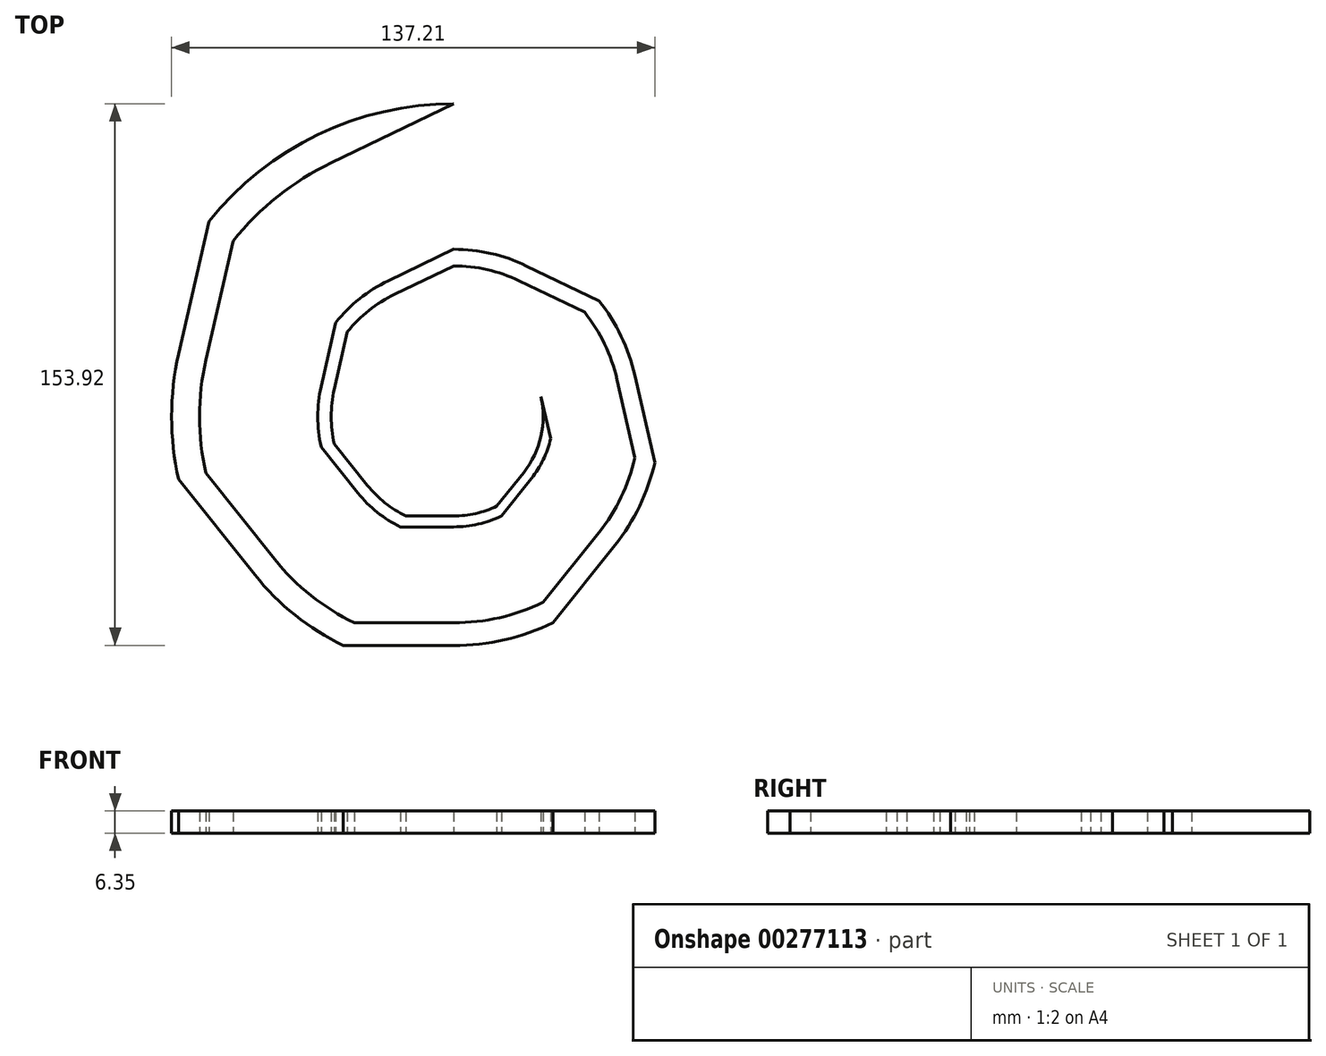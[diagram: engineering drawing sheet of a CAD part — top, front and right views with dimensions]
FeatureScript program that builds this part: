
annotation { "Feature Type Name" : "Feature", "Feature Type Description" : "" }
export const myFeature = defineFeature(function(context is Context, id is Id, definition is map)
    precondition{}
    {
        {
            var Q0;
            Q0=qCreatedBy(makeId("Top.planeOp"),FACE);
            var sketch = newSketch(context, id + "F0", { "sketchPlane" : qUnion([Q0])});
            skCircle(sketch, "E0", {"center": v(0, 0) * mm, "radius": 88.9 * mm});
            skCircle(sketch, "E1.cCircle", {"center": v(0, 0) * mm, "radius": 88.9 * mm, "construction": true});
            skLineSegment(sketch, "E1.0", {"start": v(0, 88.9) * mm, "end": v(69.5, 55.43) * mm});
            skLineSegment(sketch, "E1.1", {"start": v(69.5, 55.43) * mm, "end": v(86.67, -19.78) * mm});
            skLineSegment(sketch, "E1.2", {"start": v(86.67, -19.78) * mm, "end": v(38.57, -80.1) * mm});
            skLineSegment(sketch, "E1.3", {"start": v(38.57, -80.1) * mm, "end": v(-38.57, -80.1) * mm});
            skLineSegment(sketch, "E1.4", {"start": v(-38.57, -80.1) * mm, "end": v(-86.67, -19.78) * mm});
            skLineSegment(sketch, "E1.5", {"start": v(-86.67, -19.78) * mm, "end": v(-69.5, 55.43) * mm});
            skLineSegment(sketch, "E1.6", {"start": v(-69.5, 55.43) * mm, "end": v(0, 88.9) * mm});
            skCircle(sketch, "E2", {"center": v(0, 0) * mm, "radius": 80.1 * mm});
            skCircle(sketch, "E3.cCircle", {"center": v(0, 0) * mm, "radius": 80.1 * mm, "construction": true});
            skLineSegment(sketch, "E3.0", {"start": v(0, 80.1) * mm, "end": v(62.62, 49.94) * mm});
            skLineSegment(sketch, "E3.1", {"start": v(62.62, 49.94) * mm, "end": v(78.09, -17.82) * mm});
            skLineSegment(sketch, "E3.2", {"start": v(78.09, -17.82) * mm, "end": v(34.75, -72.16) * mm});
            skLineSegment(sketch, "E3.3", {"start": v(34.75, -72.16) * mm, "end": v(-34.75, -72.16) * mm});
            skLineSegment(sketch, "E3.4", {"start": v(-34.75, -72.16) * mm, "end": v(-78.09, -17.82) * mm});
            skLineSegment(sketch, "E3.5", {"start": v(-78.09, -17.82) * mm, "end": v(-62.62, 49.94) * mm});
            skLineSegment(sketch, "E3.6", {"start": v(-62.62, 49.94) * mm, "end": v(0, 80.1) * mm});
            skCircle(sketch, "E4", {"center": v(0, 0) * mm, "radius": 72.16 * mm});
            skCircle(sketch, "E5.cCircle", {"center": v(0, 0) * mm, "radius": 72.16 * mm, "construction": true});
            skLineSegment(sketch, "E5.0", {"start": v(0, 72.16) * mm, "end": v(56.42, 45) * mm});
            skLineSegment(sketch, "E5.1", {"start": v(56.42, 45) * mm, "end": v(70.35, -16.06) * mm});
            skLineSegment(sketch, "E5.2", {"start": v(70.35, -16.06) * mm, "end": v(31.31, -65.02) * mm});
            skLineSegment(sketch, "E5.3", {"start": v(31.31, -65.02) * mm, "end": v(-31.31, -65.02) * mm});
            skLineSegment(sketch, "E5.4", {"start": v(-31.31, -65.02) * mm, "end": v(-70.35, -16.06) * mm});
            skLineSegment(sketch, "E5.5", {"start": v(-70.35, -16.06) * mm, "end": v(-56.42, 45) * mm});
            skLineSegment(sketch, "E5.6", {"start": v(-56.42, 45) * mm, "end": v(0, 72.16) * mm});
            skCircle(sketch, "E6", {"center": v(0, 0) * mm, "radius": 65.02 * mm});
            skCircle(sketch, "E7.cCircle", {"center": v(0, 0) * mm, "radius": 65.02 * mm, "construction": true});
            skLineSegment(sketch, "E7.0", {"start": v(0, 65.02) * mm, "end": v(50.83, 40.54) * mm});
            skLineSegment(sketch, "E7.1", {"start": v(50.83, 40.54) * mm, "end": v(63.39, -14.47) * mm});
            skLineSegment(sketch, "E7.2", {"start": v(63.39, -14.47) * mm, "end": v(28.21, -58.58) * mm});
            skLineSegment(sketch, "E7.3", {"start": v(28.21, -58.58) * mm, "end": v(-28.21, -58.58) * mm});
            skLineSegment(sketch, "E7.4", {"start": v(-28.21, -58.58) * mm, "end": v(-63.39, -14.47) * mm});
            skLineSegment(sketch, "E7.5", {"start": v(-63.39, -14.47) * mm, "end": v(-50.83, 40.54) * mm});
            skLineSegment(sketch, "E7.6", {"start": v(-50.83, 40.54) * mm, "end": v(0, 65.02) * mm});
            skCircle(sketch, "E8", {"center": v(0, 0) * mm, "radius": 58.58 * mm});
            skCircle(sketch, "E9.cCircle", {"center": v(0, 0) * mm, "radius": 58.58 * mm, "construction": true});
            skLineSegment(sketch, "E9.0", {"start": v(0, 58.58) * mm, "end": v(45.8, 36.52) * mm});
            skLineSegment(sketch, "E9.1", {"start": v(45.8, 36.52) * mm, "end": v(57.11, -13.04) * mm});
            skLineSegment(sketch, "E9.2", {"start": v(57.11, -13.04) * mm, "end": v(25.42, -52.78) * mm});
            skLineSegment(sketch, "E9.3", {"start": v(25.42, -52.78) * mm, "end": v(-25.42, -52.78) * mm});
            skLineSegment(sketch, "E9.4", {"start": v(-25.42, -52.78) * mm, "end": v(-57.11, -13.04) * mm});
            skLineSegment(sketch, "E9.5", {"start": v(-57.11, -13.04) * mm, "end": v(-45.8, 36.52) * mm});
            skLineSegment(sketch, "E9.6", {"start": v(-45.8, 36.52) * mm, "end": v(0, 58.58) * mm});
            skCircle(sketch, "E10", {"center": v(0, 0) * mm, "radius": 52.78 * mm});
            skCircle(sketch, "E11.cCircle", {"center": v(0, 0) * mm, "radius": 52.78 * mm, "construction": true});
            skLineSegment(sketch, "E11.0", {"start": v(0, 52.78) * mm, "end": v(41.26, 32.9) * mm});
            skLineSegment(sketch, "E11.1", {"start": v(41.26, 32.9) * mm, "end": v(51.45, -11.74) * mm});
            skLineSegment(sketch, "E11.2", {"start": v(51.45, -11.74) * mm, "end": v(22.9, -47.55) * mm});
            skLineSegment(sketch, "E11.3", {"start": v(22.9, -47.55) * mm, "end": v(-22.9, -47.55) * mm});
            skLineSegment(sketch, "E11.4", {"start": v(-22.9, -47.55) * mm, "end": v(-51.45, -11.74) * mm});
            skLineSegment(sketch, "E11.5", {"start": v(-51.45, -11.74) * mm, "end": v(-41.26, 32.9) * mm});
            skLineSegment(sketch, "E11.6", {"start": v(-41.26, 32.9) * mm, "end": v(0, 52.78) * mm});
            skCircle(sketch, "E12", {"center": v(0, 0) * mm, "radius": 47.55 * mm});
            skCircle(sketch, "E13.cCircle", {"center": v(0, 0) * mm, "radius": 47.55 * mm, "construction": true});
            skLineSegment(sketch, "E13.0", {"start": v(0, 47.55) * mm, "end": v(37.18, 29.65) * mm});
            skLineSegment(sketch, "E13.1", {"start": v(37.18, 29.65) * mm, "end": v(46.36, -10.58) * mm});
            skLineSegment(sketch, "E13.2", {"start": v(46.36, -10.58) * mm, "end": v(20.63, -42.84) * mm});
            skLineSegment(sketch, "E13.3", {"start": v(20.63, -42.84) * mm, "end": v(-20.63, -42.84) * mm});
            skLineSegment(sketch, "E13.4", {"start": v(-20.63, -42.84) * mm, "end": v(-46.36, -10.58) * mm});
            skLineSegment(sketch, "E13.5", {"start": v(-46.36, -10.58) * mm, "end": v(-37.18, 29.65) * mm});
            skLineSegment(sketch, "E13.6", {"start": v(-37.18, 29.65) * mm, "end": v(0, 47.55) * mm});
            skCircle(sketch, "E14", {"center": v(0, 0) * mm, "radius": 42.84 * mm});
            skCircle(sketch, "E15.cCircle", {"center": v(0, 0) * mm, "radius": 42.84 * mm, "construction": true});
            skLineSegment(sketch, "E15.0", {"start": v(0, 42.84) * mm, "end": v(33.5, 26.71) * mm});
            skLineSegment(sketch, "E15.1", {"start": v(33.5, 26.71) * mm, "end": v(41.77, -9.53) * mm});
            skLineSegment(sketch, "E15.2", {"start": v(41.77, -9.53) * mm, "end": v(18.59, -38.6) * mm});
            skLineSegment(sketch, "E15.3", {"start": v(18.59, -38.6) * mm, "end": v(-18.59, -38.6) * mm});
            skLineSegment(sketch, "E15.4", {"start": v(-18.59, -38.6) * mm, "end": v(-41.77, -9.53) * mm});
            skLineSegment(sketch, "E15.5", {"start": v(-41.77, -9.53) * mm, "end": v(-33.5, 26.71) * mm});
            skLineSegment(sketch, "E15.6", {"start": v(-33.5, 26.71) * mm, "end": v(0, 42.84) * mm});
            skCircle(sketch, "E16", {"center": v(0, 0) * mm, "radius": 38.6 * mm});
            skCircle(sketch, "E17.cCircle", {"center": v(0, 0) * mm, "radius": 38.6 * mm, "construction": true});
            skLineSegment(sketch, "E17.0", {"start": v(0, 38.6) * mm, "end": v(30.18, 24.07) * mm});
            skLineSegment(sketch, "E17.1", {"start": v(30.18, 24.07) * mm, "end": v(37.63, -8.59) * mm});
            skLineSegment(sketch, "E17.2", {"start": v(37.63, -8.59) * mm, "end": v(16.75, -34.78) * mm});
            skLineSegment(sketch, "E17.3", {"start": v(16.75, -34.78) * mm, "end": v(-16.75, -34.78) * mm});
            skLineSegment(sketch, "E17.4", {"start": v(-16.75, -34.78) * mm, "end": v(-37.63, -8.59) * mm});
            skLineSegment(sketch, "E17.5", {"start": v(-37.63, -8.59) * mm, "end": v(-30.18, 24.07) * mm});
            skLineSegment(sketch, "E17.6", {"start": v(-30.18, 24.07) * mm, "end": v(0, 38.6) * mm});
            skCircle(sketch, "E18", {"center": v(0, 0) * mm, "radius": 34.78 * mm});
            skCircle(sketch, "E19.cCircle", {"center": v(0, 0) * mm, "radius": 34.78 * mm, "construction": true});
            skLineSegment(sketch, "E19.0", {"start": v(0, 34.78) * mm, "end": v(27.19, 21.68) * mm});
            skLineSegment(sketch, "E19.1", {"start": v(27.19, 21.68) * mm, "end": v(33.9, -7.74) * mm});
            skLineSegment(sketch, "E19.2", {"start": v(33.9, -7.74) * mm, "end": v(15.09, -31.33) * mm});
            skLineSegment(sketch, "E19.3", {"start": v(15.09, -31.33) * mm, "end": v(-15.09, -31.33) * mm});
            skLineSegment(sketch, "E19.4", {"start": v(-15.09, -31.33) * mm, "end": v(-33.9, -7.74) * mm});
            skLineSegment(sketch, "E19.5", {"start": v(-33.9, -7.74) * mm, "end": v(-27.19, 21.68) * mm});
            skLineSegment(sketch, "E19.6", {"start": v(-27.19, 21.68) * mm, "end": v(0, 34.78) * mm});
            skCircle(sketch, "E20", {"center": v(0, 0) * mm, "radius": 31.33 * mm});
            skCircle(sketch, "E21.cCircle", {"center": v(0, 0) * mm, "radius": 31.33 * mm, "construction": true});
            skLineSegment(sketch, "E21.0", {"start": v(0, 31.33) * mm, "end": v(24.5, 19.54) * mm});
            skLineSegment(sketch, "E21.1", {"start": v(24.5, 19.54) * mm, "end": v(30.55, -6.97) * mm});
            skLineSegment(sketch, "E21.2", {"start": v(30.55, -6.97) * mm, "end": v(13.6, -28.23) * mm});
            skLineSegment(sketch, "E21.3", {"start": v(13.6, -28.23) * mm, "end": v(-13.6, -28.23) * mm});
            skLineSegment(sketch, "E21.4", {"start": v(-13.6, -28.23) * mm, "end": v(-30.55, -6.97) * mm});
            skLineSegment(sketch, "E21.5", {"start": v(-30.55, -6.97) * mm, "end": v(-24.5, 19.54) * mm});
            skLineSegment(sketch, "E21.6", {"start": v(-24.5, 19.54) * mm, "end": v(0, 31.33) * mm});
            skCircle(sketch, "E22", {"center": v(0, 0) * mm, "radius": 28.23 * mm});
            skCircle(sketch, "E23.cCircle", {"center": v(0, 0) * mm, "radius": 28.23 * mm, "construction": true});
            skLineSegment(sketch, "E23.0", {"start": v(0, 28.23) * mm, "end": v(22.07, 17.6) * mm});
            skLineSegment(sketch, "E23.1", {"start": v(22.07, 17.6) * mm, "end": v(27.52, -6.28) * mm});
            skLineSegment(sketch, "E23.2", {"start": v(27.52, -6.28) * mm, "end": v(12.25, -25.43) * mm});
            skLineSegment(sketch, "E23.3", {"start": v(12.25, -25.43) * mm, "end": v(-12.25, -25.43) * mm});
            skLineSegment(sketch, "E23.4", {"start": v(-12.25, -25.43) * mm, "end": v(-27.52, -6.28) * mm});
            skLineSegment(sketch, "E23.5", {"start": v(-27.52, -6.28) * mm, "end": v(-22.07, 17.6) * mm});
            skLineSegment(sketch, "E23.6", {"start": v(-22.07, 17.6) * mm, "end": v(0, 28.23) * mm});
            skCircle(sketch, "E24", {"center": v(0, 0) * mm, "radius": 25.43 * mm});
            skSolve(sketch);
        }
        {
            var Q0;
            {var subQ0=sQuery(id+"F0.wireOp",EDGE,"E1.6");var subQ4=makeQuery(id+"F0.imprint","INTERSECT",VERTEX,{"derivedFrom":[subQ0,sQuery(id+"F0.wireOp",EDGE,"E2")]});Q0=makeQuery(id+"F0.imprint","IMPRINT",FACE,{"disambiguationData":[TD([[makeQuery(id+"F0.imprint","IMPRINT",EDGE,{"disambiguationData":[TD([[subQ4,1.0]])],"derivedFrom":subQ0}),1.0]])]});}
            var Q1;
            {var subQ1=sQuery(id+"F0.wireOp",EDGE,"E1.5");var subQ3=sQuery(id+"F0.wireOp",EDGE,"E2");var subQ4=makeQuery(id+"F0.imprint","INTERSECT",VERTEX,{"derivedFrom":[subQ1,subQ3]});Q1=makeQuery(id+"F0.imprint","IMPRINT",FACE,{"disambiguationData":[TD([[makeQuery(id+"F0.imprint","IMPRINT",EDGE,{"disambiguationData":[TD([[subQ4,-1.0]])],"derivedFrom":subQ1}),-1.0]])]});}
            var Q2;
            {var subQ1=sQuery(id+"F0.wireOp",EDGE,"E2");var subQ3=makeQuery(id+"F0.imprint","INTERSECT",VERTEX,{"derivedFrom":[sQuery(id+"F0.wireOp",EDGE,"E1.5"),subQ1]});Q2=makeQuery(id+"F0.imprint","IMPRINT",FACE,{"disambiguationData":[TD([[makeQuery(id+"F0.imprint","IMPRINT",EDGE,{"disambiguationData":[TD([[subQ3,1.0]])],"derivedFrom":subQ1}),1.0]])]});}
            var Q3;
            {var subQ1=sQuery(id+"F0.wireOp",EDGE,"E3.4");var subQ3=sQuery(id+"F0.wireOp",EDGE,"E4");var subQ4=makeQuery(id+"F0.imprint","INTERSECT",VERTEX,{"derivedFrom":[subQ1,subQ3]});Q3=makeQuery(id+"F0.imprint","IMPRINT",FACE,{"disambiguationData":[TD([[makeQuery(id+"F0.imprint","IMPRINT",EDGE,{"disambiguationData":[TD([[subQ4,-1.0]])],"derivedFrom":subQ1}),-1.0]])]});}
            var Q4;
            {var subQ1=sQuery(id+"F0.wireOp",EDGE,"E4");var subQ3=makeQuery(id+"F0.imprint","INTERSECT",VERTEX,{"derivedFrom":[sQuery(id+"F0.wireOp",EDGE,"E3.4"),subQ1]});Q4=makeQuery(id+"F0.imprint","IMPRINT",FACE,{"disambiguationData":[TD([[makeQuery(id+"F0.imprint","IMPRINT",EDGE,{"disambiguationData":[TD([[subQ3,1.0]])],"derivedFrom":subQ1}),1.0]])]});}
            var Q5;
            {var subQ1=sQuery(id+"F0.wireOp",EDGE,"E5.3");var subQ3=sQuery(id+"F0.wireOp",EDGE,"E6");var subQ4=makeQuery(id+"F0.imprint","INTERSECT",VERTEX,{"derivedFrom":[subQ1,subQ3]});Q5=makeQuery(id+"F0.imprint","IMPRINT",FACE,{"disambiguationData":[TD([[makeQuery(id+"F0.imprint","IMPRINT",EDGE,{"disambiguationData":[TD([[subQ4,-1.0]])],"derivedFrom":subQ1}),-1.0]])]});}
            var Q6;
            {var subQ1=sQuery(id+"F0.wireOp",EDGE,"E6");var subQ3=makeQuery(id+"F0.imprint","INTERSECT",VERTEX,{"derivedFrom":[sQuery(id+"F0.wireOp",EDGE,"E5.3"),subQ1]});Q6=makeQuery(id+"F0.imprint","IMPRINT",FACE,{"disambiguationData":[TD([[makeQuery(id+"F0.imprint","IMPRINT",EDGE,{"disambiguationData":[TD([[subQ3,1.0]])],"derivedFrom":subQ1}),1.0]])]});}
            var Q7;
            {var subQ1=sQuery(id+"F0.wireOp",EDGE,"E7.2");var subQ3=sQuery(id+"F0.wireOp",EDGE,"E8");var subQ4=makeQuery(id+"F0.imprint","INTERSECT",VERTEX,{"derivedFrom":[subQ1,subQ3]});Q7=makeQuery(id+"F0.imprint","IMPRINT",FACE,{"disambiguationData":[TD([[makeQuery(id+"F0.imprint","IMPRINT",EDGE,{"disambiguationData":[TD([[subQ4,-1.0]])],"derivedFrom":subQ1}),-1.0]])]});}
            var Q8;
            {var subQ1=sQuery(id+"F0.wireOp",EDGE,"E8");var subQ3=makeQuery(id+"F0.imprint","INTERSECT",VERTEX,{"derivedFrom":[sQuery(id+"F0.wireOp",EDGE,"E7.2"),subQ1]});Q8=makeQuery(id+"F0.imprint","IMPRINT",FACE,{"disambiguationData":[TD([[makeQuery(id+"F0.imprint","IMPRINT",EDGE,{"disambiguationData":[TD([[subQ3,1.0]])],"derivedFrom":subQ1}),1.0]])]});}
            var Q9;
            {var subQ1=sQuery(id+"F0.wireOp",EDGE,"E9.1");var subQ3=sQuery(id+"F0.wireOp",EDGE,"E10");var subQ4=makeQuery(id+"F0.imprint","INTERSECT",VERTEX,{"derivedFrom":[subQ1,subQ3]});Q9=makeQuery(id+"F0.imprint","IMPRINT",FACE,{"disambiguationData":[TD([[makeQuery(id+"F0.imprint","IMPRINT",EDGE,{"disambiguationData":[TD([[subQ4,-1.0]])],"derivedFrom":subQ1}),-1.0]])]});}
            var Q10;
            {var subQ1=sQuery(id+"F0.wireOp",EDGE,"E10");var subQ3=makeQuery(id+"F0.imprint","INTERSECT",VERTEX,{"derivedFrom":[sQuery(id+"F0.wireOp",EDGE,"E9.1"),subQ1]});Q10=makeQuery(id+"F0.imprint","IMPRINT",FACE,{"disambiguationData":[TD([[makeQuery(id+"F0.imprint","IMPRINT",EDGE,{"disambiguationData":[TD([[subQ3,-1.0]])],"derivedFrom":subQ1}),1.0]])]});}
            var Q11;
            {var subQ1=sQuery(id+"F0.wireOp",EDGE,"E11.0");var subQ3=sQuery(id+"F0.wireOp",EDGE,"E12");var subQ4=makeQuery(id+"F0.imprint","INTERSECT",VERTEX,{"derivedFrom":[subQ1,subQ3]});Q11=makeQuery(id+"F0.imprint","IMPRINT",FACE,{"disambiguationData":[TD([[makeQuery(id+"F0.imprint","IMPRINT",EDGE,{"disambiguationData":[TD([[subQ4,-1.0]])],"derivedFrom":subQ1}),-1.0]])]});}
            var Q12;
            {var subQ1=sQuery(id+"F0.wireOp",EDGE,"E12");var subQ3=makeQuery(id+"F0.imprint","INTERSECT",VERTEX,{"derivedFrom":[sQuery(id+"F0.wireOp",EDGE,"E11.0"),subQ1]});Q12=makeQuery(id+"F0.imprint","IMPRINT",FACE,{"disambiguationData":[TD([[makeQuery(id+"F0.imprint","IMPRINT",EDGE,{"disambiguationData":[TD([[subQ3,1.0]])],"derivedFrom":subQ1}),1.0]])]});}
            var Q13;
            {var subQ1=sQuery(id+"F0.wireOp",EDGE,"E13.0");var subQ3=sQuery(id+"F0.wireOp",EDGE,"E14");var subQ4=makeQuery(id+"F0.imprint","INTERSECT",VERTEX,{"derivedFrom":[subQ1,subQ3]});Q13=makeQuery(id+"F0.imprint","IMPRINT",FACE,{"disambiguationData":[TD([[makeQuery(id+"F0.imprint","IMPRINT",EDGE,{"disambiguationData":[TD([[subQ4,1.0]])],"derivedFrom":subQ1}),-1.0]])]});}
            var Q14;
            {var subQ1=sQuery(id+"F0.wireOp",EDGE,"E14");var subQ3=makeQuery(id+"F0.imprint","INTERSECT",VERTEX,{"derivedFrom":[sQuery(id+"F0.wireOp",EDGE,"E13.6"),subQ1]});Q14=makeQuery(id+"F0.imprint","IMPRINT",FACE,{"disambiguationData":[TD([[makeQuery(id+"F0.imprint","IMPRINT",EDGE,{"disambiguationData":[TD([[subQ3,1.0]])],"derivedFrom":subQ1}),1.0]])]});}
            var Q15;
            {var subQ1=sQuery(id+"F0.wireOp",EDGE,"E15.5");var subQ3=sQuery(id+"F0.wireOp",EDGE,"E16");var subQ4=makeQuery(id+"F0.imprint","INTERSECT",VERTEX,{"derivedFrom":[subQ1,subQ3]});Q15=makeQuery(id+"F0.imprint","IMPRINT",FACE,{"disambiguationData":[TD([[makeQuery(id+"F0.imprint","IMPRINT",EDGE,{"disambiguationData":[TD([[subQ4,-1.0]])],"derivedFrom":subQ1}),-1.0]])]});}
            var Q16;
            {var subQ1=sQuery(id+"F0.wireOp",EDGE,"E16");var subQ3=makeQuery(id+"F0.imprint","INTERSECT",VERTEX,{"derivedFrom":[sQuery(id+"F0.wireOp",EDGE,"E15.5"),subQ1]});Q16=makeQuery(id+"F0.imprint","IMPRINT",FACE,{"disambiguationData":[TD([[makeQuery(id+"F0.imprint","IMPRINT",EDGE,{"disambiguationData":[TD([[subQ3,1.0]])],"derivedFrom":subQ1}),1.0]])]});}
            var Q17;
            {var subQ1=sQuery(id+"F0.wireOp",EDGE,"E17.4");var subQ3=sQuery(id+"F0.wireOp",EDGE,"E18");var subQ4=makeQuery(id+"F0.imprint","INTERSECT",VERTEX,{"derivedFrom":[subQ1,subQ3]});Q17=makeQuery(id+"F0.imprint","IMPRINT",FACE,{"disambiguationData":[TD([[makeQuery(id+"F0.imprint","IMPRINT",EDGE,{"disambiguationData":[TD([[subQ4,-1.0]])],"derivedFrom":subQ1}),-1.0]])]});}
            var Q18;
            {var subQ1=sQuery(id+"F0.wireOp",EDGE,"E18");var subQ3=makeQuery(id+"F0.imprint","INTERSECT",VERTEX,{"derivedFrom":[sQuery(id+"F0.wireOp",EDGE,"E17.4"),subQ1]});Q18=makeQuery(id+"F0.imprint","IMPRINT",FACE,{"disambiguationData":[TD([[makeQuery(id+"F0.imprint","IMPRINT",EDGE,{"disambiguationData":[TD([[subQ3,1.0]])],"derivedFrom":subQ1}),1.0]])]});}
            var Q19;
            {var subQ1=sQuery(id+"F0.wireOp",EDGE,"E19.3");var subQ3=sQuery(id+"F0.wireOp",EDGE,"E20");var subQ4=makeQuery(id+"F0.imprint","INTERSECT",VERTEX,{"derivedFrom":[subQ1,subQ3]});Q19=makeQuery(id+"F0.imprint","IMPRINT",FACE,{"disambiguationData":[TD([[makeQuery(id+"F0.imprint","IMPRINT",EDGE,{"disambiguationData":[TD([[subQ4,-1.0]])],"derivedFrom":subQ1}),-1.0]])]});}
            var Q20;
            {var subQ1=sQuery(id+"F0.wireOp",EDGE,"E20");var subQ3=makeQuery(id+"F0.imprint","INTERSECT",VERTEX,{"derivedFrom":[sQuery(id+"F0.wireOp",EDGE,"E19.3"),subQ1]});Q20=makeQuery(id+"F0.imprint","IMPRINT",FACE,{"disambiguationData":[TD([[makeQuery(id+"F0.imprint","IMPRINT",EDGE,{"disambiguationData":[TD([[subQ3,1.0]])],"derivedFrom":subQ1}),1.0]])]});}
            var Q21;
            {var subQ1=sQuery(id+"F0.wireOp",EDGE,"E21.2");var subQ3=sQuery(id+"F0.wireOp",EDGE,"E22");var subQ4=makeQuery(id+"F0.imprint","INTERSECT",VERTEX,{"derivedFrom":[subQ1,subQ3]});Q21=makeQuery(id+"F0.imprint","IMPRINT",FACE,{"disambiguationData":[TD([[makeQuery(id+"F0.imprint","IMPRINT",EDGE,{"disambiguationData":[TD([[subQ4,-1.0]])],"derivedFrom":subQ1}),-1.0]])]});}
            var Q22;
            {var subQ1=sQuery(id+"F0.wireOp",EDGE,"E22");var subQ3=makeQuery(id+"F0.imprint","INTERSECT",VERTEX,{"derivedFrom":[sQuery(id+"F0.wireOp",EDGE,"E21.2"),subQ1]});Q22=makeQuery(id+"F0.imprint","IMPRINT",FACE,{"disambiguationData":[TD([[makeQuery(id+"F0.imprint","IMPRINT",EDGE,{"disambiguationData":[TD([[subQ3,1.0]])],"derivedFrom":subQ1}),1.0]])]});}
            var Q23;
            {var subQ1=sQuery(id+"F0.wireOp",EDGE,"E23.1");var subQ3=sQuery(id+"F0.wireOp",EDGE,"E24");var subQ4=makeQuery(id+"F0.imprint","INTERSECT",VERTEX,{"derivedFrom":[subQ1,subQ3]});Q23=makeQuery(id+"F0.imprint","IMPRINT",FACE,{"disambiguationData":[TD([[makeQuery(id+"F0.imprint","IMPRINT",EDGE,{"disambiguationData":[TD([[subQ4,1.0]])],"derivedFrom":subQ3}),-1.0]])]});}
            extrude(context, id + "F1", {"entities" : qUnion([Q0, Q1, Q2, Q3, Q4, Q5, Q6, Q7, Q8, Q9, Q10, Q11, Q12, Q13, Q14, Q15, Q16, Q17, Q18, Q19, Q20, Q21, Q22, Q23]), "depth" : 6.35 * mm});
        }
    });
